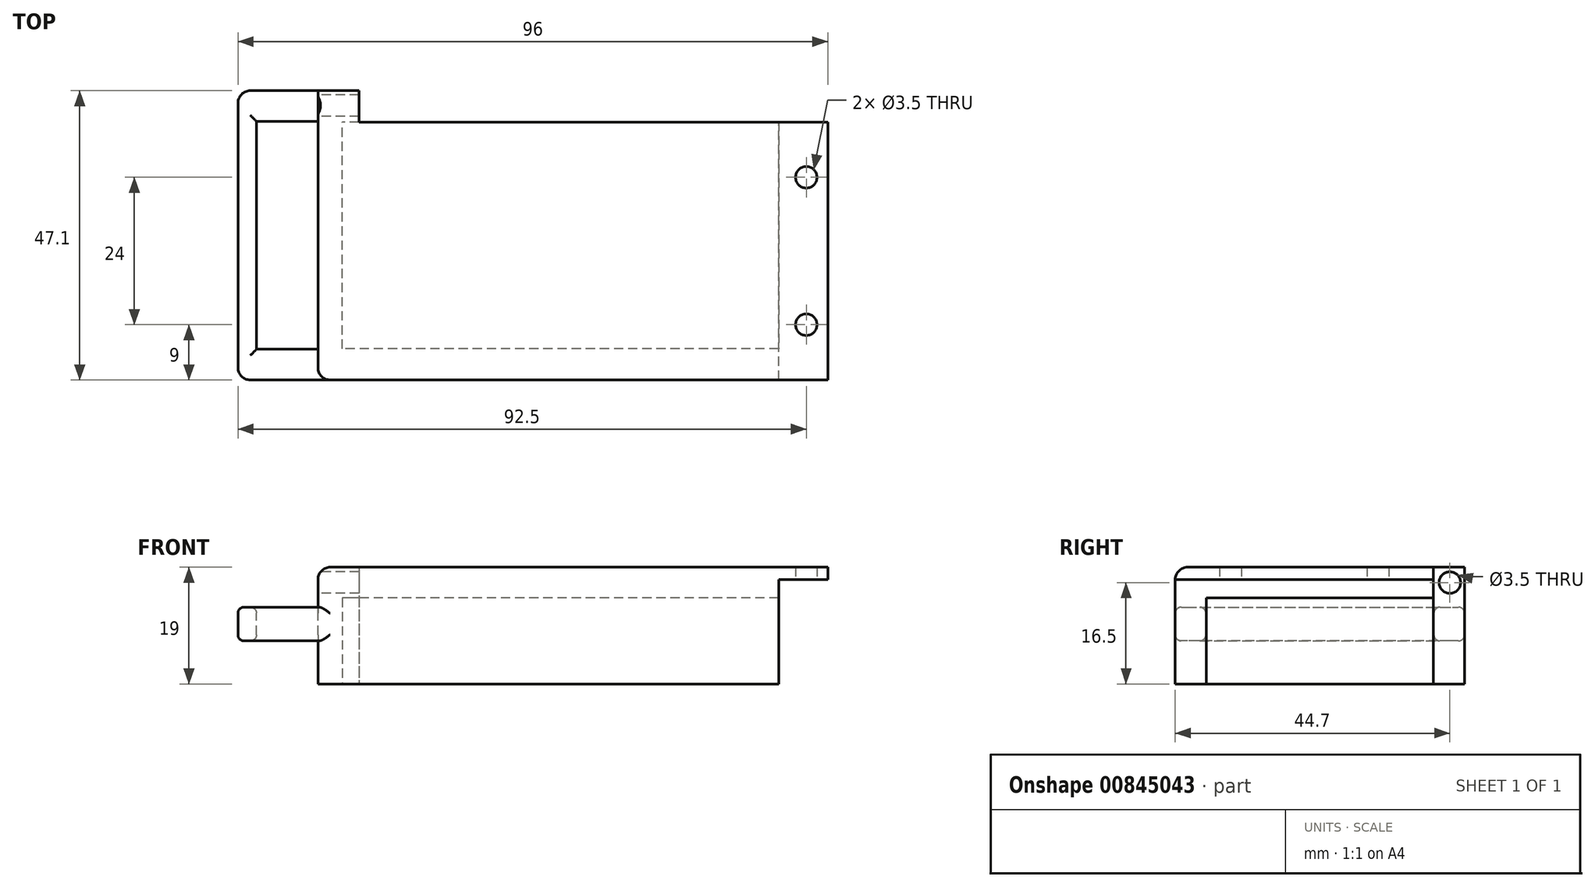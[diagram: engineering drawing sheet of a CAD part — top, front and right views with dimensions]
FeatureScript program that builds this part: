
annotation { "Feature Type Name" : "Feature", "Feature Type Description" : "" }
export const myFeature = defineFeature(function(context is Context, id is Id, definition is map)
    precondition{}
    {
        {
            var Q0;
            Q0=qCreatedBy(makeId("Top.planeOp"),FACE);
            var sketch = newSketch(context, id + "F0", { "sketchPlane" : qUnion([Q0])});
            skLineSegment(sketch, "E0", {"start": v(0, 0) * mm, "end": v(0, 42) * mm});
            skLineSegment(sketch, "E1", {"start": v(0, 42) * mm, "end": v(-83, 42) * mm});
            skLineSegment(sketch, "E2", {"start": v(-83, 42) * mm, "end": v(-83, 0) * mm});
            skLineSegment(sketch, "E3", {"start": v(-83, 0) * mm, "end": v(0, 0) * mm});
            skSolve(sketch);
        }
        {
            var Q0;
            Q0 = qSketchRegion(id + "F0", true);
            extrude(context, id + "F1", {"entities" : qUnion([Q0]), "depth" : 19 * mm, "offsetDistance" : 25 * mm});
        }
        {
            var Q0;
            Q0=qCreatedBy(makeId("Top.planeOp"),FACE);
            var sketch = newSketch(context, id + "F2", { "sketchPlane" : qUnion([Q0])});
            skLineSegment(sketch, "E4", {"start": v(0, 0) * mm, "end": v(0, 5.09) * mm, "construction": true});
            skLineSegment(sketch, "E5", {"start": v(0, 5.09) * mm, "end": v(-79, 5.09) * mm});
            skLineSegment(sketch, "E6", {"start": v(-79, 5.09) * mm, "end": v(-79, 42.05) * mm});
            skLineSegment(sketch, "E7", {"start": v(-79, 42.05) * mm, "end": v(0, 42.05) * mm});
            skLineSegment(sketch, "E8", {"start": v(0, 42.05) * mm, "end": v(0, 5.09) * mm});
            skSolve(sketch);
        }
        {
            var Q0;
            Q0 = qSketchRegion(id + "F2", true);
            extrude(context, id + "F3", {"entities" : qUnion([Q0]), "operationType" : NewBodyOperationType.REMOVE, "depth" : 14 * mm, "offsetDistance" : 25 * mm});
        }
        {
            var Q0;
            Q0=qCreatedBy(makeId("Top.planeOp"),FACE);
            var sketch = newSketch(context, id + "F4", { "sketchPlane" : qUnion([Q0])});
            skLineSegment(sketch, "E9", {"start": v(0, 0) * mm, "end": v(-8, 0) * mm});
            skLineSegment(sketch, "E10", {"start": v(-8, 0) * mm, "end": v(-8, 42) * mm});
            skLineSegment(sketch, "E11", {"start": v(-8, 42) * mm, "end": v(0, 42) * mm});
            skLineSegment(sketch, "E12", {"start": v(0, 42) * mm, "end": v(0, 0) * mm});
            skSolve(sketch);
        }
        {
            var Q0;
            Q0 = qSketchRegion(id + "F4", true);
            extrude(context, id + "F5", {"entities" : qUnion([Q0]), "operationType" : NewBodyOperationType.REMOVE, "depth" : 17 * mm, "offsetDistance" : 25 * mm});
        }
        {
            var Q0;
            Q0=qCreatedBy(makeId("Top.planeOp"),FACE);
            var sketch = newSketch(context, id + "F6", { "sketchPlane" : qUnion([Q0])});
            skLineSegment(sketch, "E13", {"start": v(0, 0) * mm, "end": v(-3.5, 0) * mm});
            skLineSegment(sketch, "E14", {"start": v(-3.5, 0) * mm, "end": v(-3.5, 9) * mm});
            skLineSegment(sketch, "E15", {"start": v(-3.5, 9) * mm, "end": v(-3.5, 33) * mm});
            skLineSegment(sketch, "E16", {"start": v(-3.5, 33) * mm, "end": v(-3.5, 42) * mm});
            skCircle(sketch, "E17", {"center": v(-3.5, 33) * mm, "radius": 1.75 * mm});
            skCircle(sketch, "E18", {"center": v(-3.5, 9) * mm, "radius": 1.75 * mm});
            skSolve(sketch);
        }
        {
            var Q0;
            Q0 = qSketchRegion(id + "F6", true);
            extrude(context, id + "F7", {"entities" : qUnion([Q0]), "operationType" : NewBodyOperationType.REMOVE, "depth" : 25 * mm, "offsetDistance" : 25 * mm});
        }
        {
            var Q0;
            Q0=makeQuery(id+"F1.opExtrude","SWEPT_FACE",FACE,{"disambiguationData":[OSD([sQuery(id+"F0.wireOp",EDGE,"E1")])]});
            var sketch = newSketch(context, id + "F8", { "sketchPlane" : qUnion([Q0])});
            skLineSegment(sketch, "E19", {"start": v(0, 0) * mm, "end": v(83, 0) * mm, "construction": true});
            skLineSegment(sketch, "E20", {"start": v(83, 0) * mm, "end": v(83, 19) * mm});
            skLineSegment(sketch, "E21", {"start": v(83, 19) * mm, "end": v(76.3, 19) * mm});
            skLineSegment(sketch, "E22", {"start": v(76.3, 19) * mm, "end": v(76.3, 0) * mm});
            skLineSegment(sketch, "E23", {"start": v(76.3, 0) * mm, "end": v(83, 0) * mm});
            skSolve(sketch);
        }
        {
            var Q0;
            Q0 = qSketchRegion(id + "F8", true);
            extrude(context, id + "F9", {"entities" : qUnion([Q0]), "operationType" : NewBodyOperationType.ADD, "depth" : 5.1 * mm, "offsetDistance" : 25 * mm});
        }
        {
            var Q0;
            Q0=makeQuery(id+"F9.boolean.opBoolean","MERGE",FACE,{"derivedFrom":[makeQuery(id+"F1.opExtrude","SWEPT_FACE",FACE,{"disambiguationData":[OSD([sQuery(id+"F0.wireOp",EDGE,"E2")])]}),makeQuery(id+"F9.opExtrude","SWEPT_FACE",FACE,{"disambiguationData":[OSD([sQuery(id+"F8.wireOp",EDGE,"E20")])]})]});
            var sketch = newSketch(context, id + "F10", { "sketchPlane" : qUnion([Q0])});
            skLineSegment(sketch, "E24", {"start": v(0, 0) * mm, "end": v(0, 19) * mm, "construction": true});
            skLineSegment(sketch, "E25", {"start": v(0, 19) * mm, "end": v(-47.1, 19) * mm, "construction": true});
            skLineSegment(sketch, "E26", {"start": v(-47.1, 19) * mm, "end": v(-47.1, 16.5) * mm, "construction": true});
            skLineSegment(sketch, "E27", {"start": v(-47.1, 16.5) * mm, "end": v(-44.7, 16.5) * mm, "construction": true});
            skCircle(sketch, "E28", {"center": v(-44.7, 16.5) * mm, "radius": 1.75 * mm});
            skSolve(sketch);
        }
        {
            var Q0;
            Q0 = qSketchRegion(id + "F10", true);
            extrude(context, id + "F11", {"entities" : qUnion([Q0]), "operationType" : NewBodyOperationType.REMOVE, "oppositeDirection" : true, "depth" : 7 * mm, "offsetDistance" : 25 * mm});
        }
        {
            var Q0;
            Q0=makeQuery(id+"F9.boolean.opBoolean","MERGE",FACE,{"derivedFrom":[makeQuery(id+"F1.opExtrude","SWEPT_FACE",FACE,{"disambiguationData":[OSD([sQuery(id+"F0.wireOp",EDGE,"E2")])]}),makeQuery(id+"F9.opExtrude","SWEPT_FACE",FACE,{"disambiguationData":[OSD([sQuery(id+"F8.wireOp",EDGE,"E20")])]})]});
            var sketch = newSketch(context, id + "F12", { "sketchPlane" : qUnion([Q0])});
            skLineSegment(sketch, "E29", {"start": v(0, 0) * mm, "end": v(0, 7) * mm, "construction": true});
            skLineSegment(sketch, "E30", {"start": v(0, 7) * mm, "end": v(0, 12.5) * mm});
            skLineSegment(sketch, "E31", {"start": v(0, 12.5) * mm, "end": v(-5, 12.5) * mm});
            skLineSegment(sketch, "E32", {"start": v(-5, 12.5) * mm, "end": v(-5, 7) * mm});
            skLineSegment(sketch, "E33", {"start": v(-5, 7) * mm, "end": v(0, 7) * mm});
            skLineSegment(sketch, "E34", {"start": v(-5, 7) * mm, "end": v(-42.1, 7) * mm, "construction": true});
            skLineSegment(sketch, "E35", {"start": v(-42.1, 7) * mm, "end": v(-42.1, 12.5) * mm});
            skLineSegment(sketch, "E36", {"start": v(-42.1, 12.5) * mm, "end": v(-47.1, 12.5) * mm});
            skLineSegment(sketch, "E37", {"start": v(-47.1, 12.5) * mm, "end": v(-47.1, 7) * mm});
            skLineSegment(sketch, "E38", {"start": v(-47.1, 7) * mm, "end": v(-42.1, 7) * mm});
            skSolve(sketch);
        }
        {
            var Q0;
            Q0 = qSketchRegion(id + "F12", true);
            extrude(context, id + "F13", {"entities" : qUnion([Q0]), "operationType" : NewBodyOperationType.ADD, "depth" : 13 * mm, "offsetDistance" : 25 * mm});
        }
        {
            var Q0;
            Q0=makeQuery(id+"F13.opExtrude","SWEPT_FACE",FACE,{"disambiguationData":[OSD([sQuery(id+"F12.wireOp",EDGE,"E35")])]});
            var sketch = newSketch(context, id + "F14", { "sketchPlane" : qUnion([Q0])});
            skLineSegment(sketch, "E39.bottom", {"start": v(-96, 7) * mm, "end": v(-93, 7) * mm});
            skLineSegment(sketch, "E39.top", {"start": v(-96, 12.5) * mm, "end": v(-93, 12.5) * mm});
            skLineSegment(sketch, "E39.left", {"start": v(-96, 7) * mm, "end": v(-96, 12.5) * mm});
            skLineSegment(sketch, "E39.right", {"start": v(-93, 7) * mm, "end": v(-93, 12.5) * mm});
            skSolve(sketch);
        }
        {
            var Q0;
            Q0 = qSketchRegion(id + "F14", true);
            extrude(context, id + "F15", {"entities" : qUnion([Q0]), "operationType" : NewBodyOperationType.ADD, "depth" : 40 * mm, "offsetDistance" : 25 * mm});
        }
        {
            var Q0;
            {var subQ0=sQuery(id+"F0.wireOp",EDGE,"E3");var subQ1=sQuery(id+"F0.wireOp",EDGE,"E2");Q0=makeQuery(id+"F13.boolean.opBoolean","SPLIT",EDGE,{"disambiguationData":[TD([makeQuery(id+"F9.opExtrude","SWEPT_FACE",FACE,{"disambiguationData":[OSD([sQuery(id+"F8.wireOp",EDGE,"E21")])]})])],"derivedFrom":makeQuery(id+"F1.opExtrude","SWEPT_EDGE",EDGE,{"disambiguationData":[OSD([subQ1,subQ0])]})});}
            var Q1;
            {var subQ0=sQuery(id+"F0.wireOp",EDGE,"E3");var subQ1=sQuery(id+"F0.wireOp",EDGE,"E2");Q1=makeQuery(id+"F13.boolean.opBoolean","SPLIT",EDGE,{"disambiguationData":[TD([makeQuery(id+"F9.opExtrude","SWEPT_FACE",FACE,{"disambiguationData":[OSD([sQuery(id+"F8.wireOp",EDGE,"E23")])]})])],"derivedFrom":makeQuery(id+"F1.opExtrude","SWEPT_EDGE",EDGE,{"disambiguationData":[OSD([subQ1,subQ0])]})});}
            var Q2;
            Q2=makeQuery(id+"F9.boolean.opBoolean","MERGE",EDGE,{"derivedFrom":[makeQuery(id+"F1.opExtrude","CAP_EDGE",EDGE,{"disambiguationData":[OSD([sQuery(id+"F0.wireOp",EDGE,"E2")])],"isStart":false}),makeQuery(id+"F9.opExtrude","SWEPT_EDGE",EDGE,{"disambiguationData":[OSD([sQuery(id+"F8.wireOp",EDGE,"E20"),sQuery(id+"F8.wireOp",EDGE,"E21")])]})]});
            var Q3;
            Q3=makeQuery(id+"F1.opExtrude","CAP_EDGE",EDGE,{"disambiguationData":[OSD([sQuery(id+"F0.wireOp",EDGE,"E3")])],"isStart":false});
            var Q4;
            Q4=makeQuery(id+"F13.opExtrude","CAP_EDGE",EDGE,{"disambiguationData":[OSD([sQuery(id+"F12.wireOp",EDGE,"E30")])],"isStart":false});
            var Q5;
            Q5=makeQuery(id+"F13.opExtrude","CAP_EDGE",EDGE,{"disambiguationData":[OSD([sQuery(id+"F12.wireOp",EDGE,"E37")])],"isStart":false});
            fillet(context, id + "F16", {"entities" : qUnion([Q0, Q1, Q2, Q3, Q4, Q5]), "radius" : 2 * mm, "tangentPropagation" : true, "allowEdgeOverflow" : false});
        }
        {
            var Q0;
            Q0=makeQuery(id+"F13.opExtrude","SWEPT_EDGE",EDGE,{"disambiguationData":[OSD([sQuery(id+"F0.wireOp",EDGE,"E2"),sQuery(id+"F0.wireOp",EDGE,"E3"),sQuery(id+"F12.wireOp",EDGE,"E30"),sQuery(id+"F12.wireOp",EDGE,"E31")])]});
            var Q1;
            Q1=makeQuery(id+"F13.opExtrude","SWEPT_EDGE",EDGE,{"disambiguationData":[OSD([sQuery(id+"F0.wireOp",EDGE,"E2"),sQuery(id+"F0.wireOp",EDGE,"E3"),sQuery(id+"F12.wireOp",EDGE,"E30"),sQuery(id+"F12.wireOp",EDGE,"E33")])]});
            var Q2;
            Q2=makeQuery(id+"F13.opExtrude","SWEPT_EDGE",EDGE,{"disambiguationData":[OSD([sQuery(id+"F12.wireOp",EDGE,"E31"),sQuery(id+"F12.wireOp",EDGE,"E32")])]});
            var Q3;
            Q3=makeQuery(id+"F13.opExtrude","SWEPT_EDGE",EDGE,{"disambiguationData":[OSD([sQuery(id+"F12.wireOp",EDGE,"E32"),sQuery(id+"F12.wireOp",EDGE,"E33")])]});
            var Q4;
            Q4=makeQuery(id+"F13.opExtrude","SWEPT_EDGE",EDGE,{"disambiguationData":[OSD([sQuery(id+"F12.wireOp",EDGE,"E35"),sQuery(id+"F12.wireOp",EDGE,"E38")])]});
            var Q5;
            Q5=makeQuery(id+"F13.opExtrude","SWEPT_EDGE",EDGE,{"disambiguationData":[OSD([sQuery(id+"F12.wireOp",EDGE,"E35"),sQuery(id+"F12.wireOp",EDGE,"E36")])]});
            var Q6;
            Q6=makeQuery(id+"F15.opExtrude","SWEPT_EDGE",EDGE,{"disambiguationData":[OSD([sQuery(id+"F12.wireOp",EDGE,"E35"),sQuery(id+"F12.wireOp",EDGE,"E36"),sQuery(id+"F14.wireOp",EDGE,"E39.top"),sQuery(id+"F14.wireOp",EDGE,"E39.right")])]});
            var Q7;
            Q7=makeQuery(id+"F15.opExtrude","SWEPT_EDGE",EDGE,{"disambiguationData":[OSD([sQuery(id+"F12.wireOp",EDGE,"E35"),sQuery(id+"F12.wireOp",EDGE,"E38"),sQuery(id+"F14.wireOp",EDGE,"E39.bottom"),sQuery(id+"F14.wireOp",EDGE,"E39.right")])]});
            var Q8;
            Q8=makeQuery(id+"F13.opExtrude","CAP_EDGE",EDGE,{"disambiguationData":[OSD([sQuery(id+"F12.wireOp",EDGE,"E32")])],"isStart":true});
            var Q9;
            Q9=makeQuery(id+"F13.opExtrude","CAP_EDGE",EDGE,{"disambiguationData":[OSD([sQuery(id+"F12.wireOp",EDGE,"E35")])],"isStart":true});
            fillet(context, id + "F17", {"entities" : qUnion([Q0, Q1, Q2, Q3, Q4, Q5, Q6, Q7, Q8, Q9]), "radius" : 1 * mm, "tangentPropagation" : true, "allowEdgeOverflow" : false});
        }
    });
